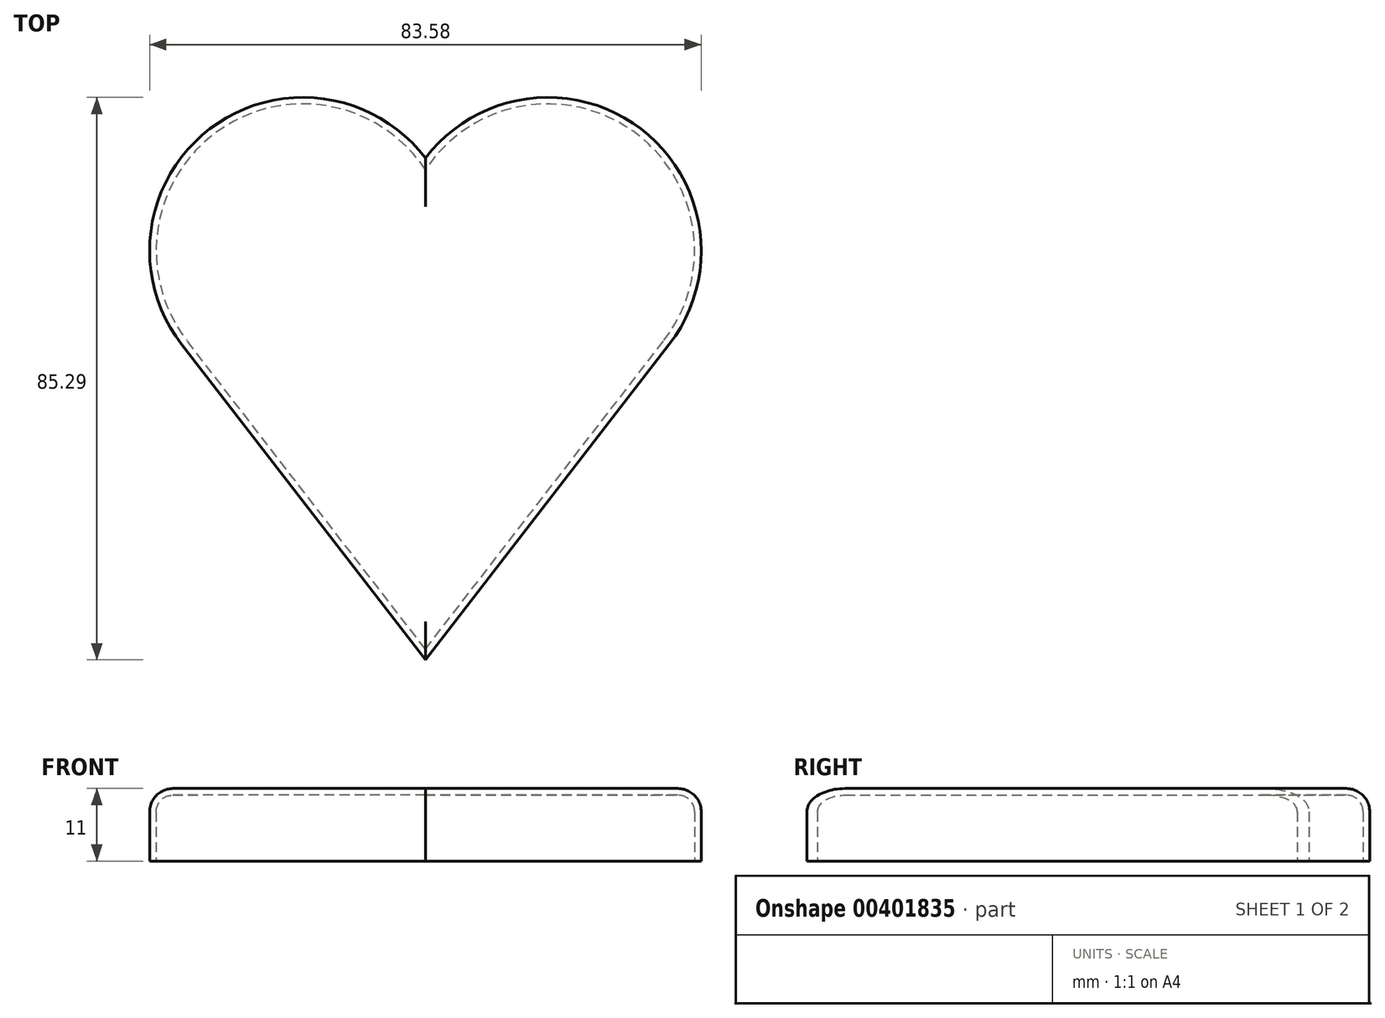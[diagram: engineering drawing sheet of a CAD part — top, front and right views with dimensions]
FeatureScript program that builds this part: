
annotation { "Feature Type Name" : "Feature", "Feature Type Description" : "" }
export const myFeature = defineFeature(function(context is Context, id is Id, definition is map)
    precondition{}
    {
        {
            var Q0;
            Q0=qCreatedBy(makeId("Top.planeOp"),FACE);
            var sketch = newSketch(context, id + "F0", { "sketchPlane" : qUnion([Q0])});
            skLineSegment(sketch, "E0", {"start": v(0, -46.8) * mm, "end": v(36.15, 0) * mm});
            skArc(sketch, "E1", {"start": v(36.15, 0) * mm, "mid": v(31.5, 31.69) * mm, "end": v(0, 25.9) * mm});
            skLineSegment(sketch, "E2", {"start": v(0, -46.8) * mm, "end": v(-36.15, 0) * mm});
            skArc(sketch, "E3", {"start": v(-36.15, 0) * mm, "mid": v(-31.5, 31.69) * mm, "end": v(0, 25.9) * mm});
            skSolve(sketch);
        }
        {
            var Q0;
            Q0=makeQuery(id+"F0.imprint","IMPRINT",FACE,{"disambiguationData":[TD([[makeQuery(id+"F0.imprint","IMPRINT",EDGE,{"derivedFrom":sQuery(id+"F0.wireOp",EDGE,"E0")}),1.0]])]});
            extrude(context, id + "F1", {"entities" : qUnion([Q0]), "depth" : 10 * mm});
        }
        {
            var Q0;
            Q0=makeQuery(id+"F1.opExtrude","CAP_FACE",FACE,{"disambiguationData":[OSD([sQuery(id+"F0.wireOp",EDGE,"E0"),sQuery(id+"F0.wireOp",EDGE,"E1"),sQuery(id+"F0.wireOp",EDGE,"E2"),sQuery(id+"F0.wireOp",EDGE,"E3")])],"isStart":false});
            fillet(context, id + "F2", {"entities" : qUnion([Q0]), "radius" : 2.54 * mm, "tangentPropagation" : true, "allowEdgeOverflow" : false});
        }
        {
            var Q0;
            Q0=makeQuery(id+"F1.opExtrude","CAP_FACE",FACE,{"disambiguationData":[OSD([sQuery(id+"F0.wireOp",EDGE,"E0"),sQuery(id+"F0.wireOp",EDGE,"E1"),sQuery(id+"F0.wireOp",EDGE,"E2"),sQuery(id+"F0.wireOp",EDGE,"E3")])],"isStart":true});
            shell(context, id + "F3", {"entities" : qUnion([Q0]), "thickness" : 1 * mm, "oppositeDirection" : true});
        }
    });
